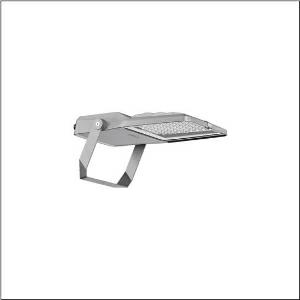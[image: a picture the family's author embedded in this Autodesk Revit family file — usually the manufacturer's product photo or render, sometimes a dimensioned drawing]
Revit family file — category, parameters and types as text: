
# Revit family: floodlight_fl_21_mini___pl33t_5xa7772c2f1a_88d6
name_source: partatom
category: Lighting Fixtures
units: mm (PartAtom-declared; Revit-internal decimal feet)

## family parameters
Cut with Voids When Loaded = No
Host = Face
Light Source = No
Part Type = Normal
Room Calculation Point = No
Round Connector Dimension = Use Diameter
Shared = No

## types (1)
- --- (1 x LED, 12060 lm, 87.2 W, 3000K)
    Apparent Load = 87 VA
    CIE Flux Codes = 26 75 99 100 100
    Color Rendering = 70
    Color Temperature = 3000K
    Default Elevation = 1800 mm
    Description = Floodlight FL 21 mini, floodlight, primary light control with lens, of PMMA, primary optical cover: protective disc, of toughened safety glass, transparent, light distribution: PL33T, light emission: direct distribution, installation type: surface-mounted, LED, High Power LED, rated luminous flux: 12.060lm, luminous efficacy: 138lm/W, light colour: 730, colour temperature: 3000K, control gear: ECG iQ, control: Street-Remote, Auto-Match, Temp-Guard, Night-Set, Smart-Wire, Desk-Remote (wireless, voltage-free reading and setting of iQ features in the workshop via application-optimized NFC function/RFID function), optimised constant luminous flux control (CLO 2.0), with terminal, 6-pole, mains connection: 220..240V, AC, 50/60Hz, start of lifetime: 87W, end of lifetime: 92W, reduction: 40W, luminaire housing, of diecast aluminium, powder-coated, Siteco® metallic grey (DB 702S), corrosivity category C5 according to DIN EN ISO 12944, mounting bracket, of steel, galvanised, powder-coated, Siteco® metallic grey (DB 702S), protection rating (complete): IP66, insulation class (complete): insulation class II (safety insulation), certification: CE, ENEC, VDE, protection symbol: D, impact resistance: IK08, permissible operating ambient temperature: -40..+40°C, permissible operating ambient temperature for outdoor applications: -40..+50°C, standard: DIN EN 12944, packaging unit: 1 piece

Light Distribution: PL33T
    Height = 70 mm
    Lamp = 1 x LED
    Lamp Light Flux = 12060 lm
    Lamp Power = 87.2 W
    Lamp count = 1
    Length = 485 mm
    Luminous efficacy = 138 lm/W
    Manufacturer = Siteco
    ModVariant = No
    Model = 5XA7772C2F1A
    Number of Poles = 1
    OnlyDefault = Yes
    Power Factor = 1
    Product Name = Floodlight FL 21 mini | PL33T
    Product group = floodlight | pylon top
    ProductGroupID = 6101
    Protection Class = Protection class II
    Protection Degree = IP 66
    RLX_Detail_Level = 1
    RlxData = <blob elided: 96041 chars, md5=05092e52>
    Socket = socket
    Standby Power = 0 W
    System Light Flux = 12060 lm
    System Power = 87 W
    Type Comments = factory setting: luminous flux: 100 % | dim-lin: 254 | 456 mA
    Type Image = l_1006845.jpg
    URL = http://relux.com
    VarID = @adj_059585
    Voltage = 0 V
    Weight = 0.00 kg
    Width = 337 mm

## geometry (parser evidence)
native form markers: Blend x4, Sweep x13
no freeform markers — native parametric forms only
